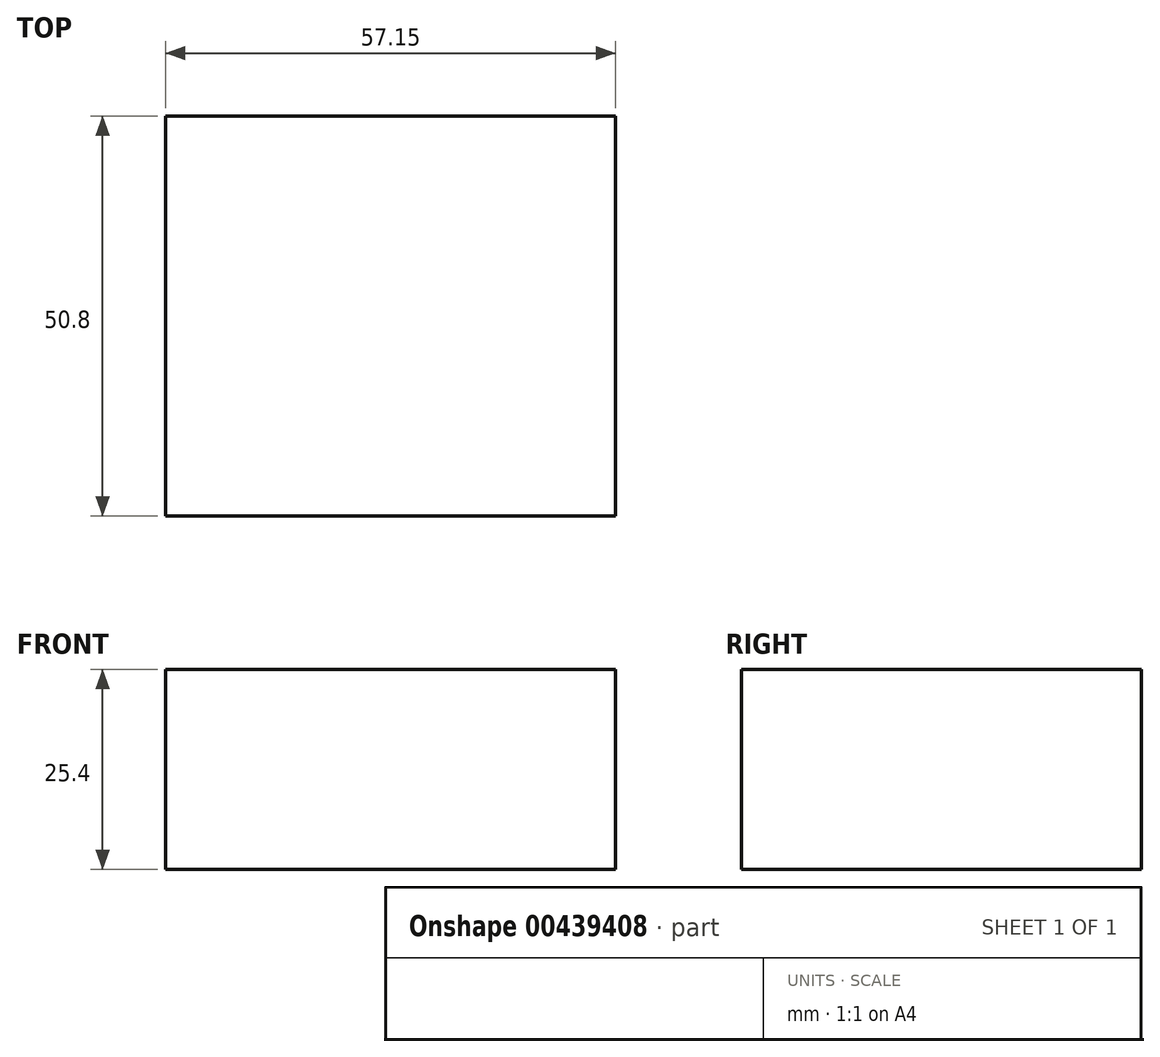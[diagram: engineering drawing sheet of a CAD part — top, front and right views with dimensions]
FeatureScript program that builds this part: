
annotation { "Feature Type Name" : "Feature", "Feature Type Description" : "" }
export const myFeature = defineFeature(function(context is Context, id is Id, definition is map)
    precondition{}
    {
        {
            var Q0;
            Q0=qCreatedBy(makeId("Top.planeOp"),FACE);
            var sketch = newSketch(context, id + "F0", { "sketchPlane" : qUnion([Q0])});
            skLineSegment(sketch, "E0.bottom", {"start": v(-29.1, 0) * mm, "end": v(28.06, 0) * mm});
            skLineSegment(sketch, "E0.top", {"start": v(-29.1, -50.8) * mm, "end": v(28.06, -50.8) * mm});
            skLineSegment(sketch, "E0.left", {"start": v(-29.1, 0) * mm, "end": v(-29.1, -50.8) * mm});
            skLineSegment(sketch, "E0.right", {"start": v(28.06, 0) * mm, "end": v(28.06, -50.8) * mm});
            skSolve(sketch);
        }
        {
            var Q0;
            Q0=makeQuery(id+"F0.imprint","IMPRINT",FACE,{"disambiguationData":[TD([[makeQuery(id+"F0.imprint","IMPRINT",EDGE,{"derivedFrom":sQuery(id+"F0.wireOp",EDGE,"E0.bottom")}),-1.0]])]});
            extrude(context, id + "F1", {"entities" : qUnion([Q0]), "depth" : 25.4 * mm});
        }
    });
